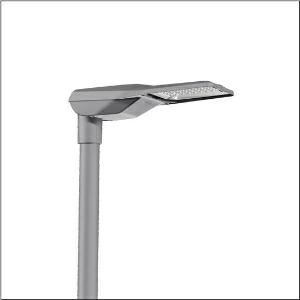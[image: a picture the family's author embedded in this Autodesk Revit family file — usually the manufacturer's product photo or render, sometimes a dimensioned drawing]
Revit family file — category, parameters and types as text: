
# Revit family: streetlight_sl_21_iq_mini___st1_0a_5xe2d21g08hb_8dd2
name_source: partatom
category: Lighting Fixtures
units: mm (PartAtom-declared; Revit-internal decimal feet)

## family parameters
Cut with Voids When Loaded = No
Host = Face
Light Source = No
Part Type = Normal
Room Calculation Point = No
Round Connector Dimension = Use Diameter
Shared = No

## types (1)
- --- (1 x LED, 7830 lm, 70.9 W, 2200K)
    Apparent Load = 71 VA
    CIE Flux Codes = 37 72 97 100 100
    Color Rendering = 70
    Color Temperature = 2200K
    Default Elevation = 1800 mm
    Description = Streetlight SL 21 iQ mini, mast luminaire, primary light control with lens, of PMMA, primary optical cover: cover, of toughened safety glass, transparent, light distribution: ST1.0a, light emission: direct distribution, primary light characteristic: asymmetric, installation type: post-top, side-entry, LED, High Power LED, rated luminous flux: 7.830lm, luminous efficacy: 110lm/W, light colour: 722, colour temperature: 2200K, control: Street-Remote, Auto-Match, Temp-Guard, Lumen-Switch, Night-Set, Smart-Wire, Light-Fading, Desk-Remote (wireless, voltage-free reading and setting of iQ features in the workshop via application-optimized NFC function/RFID function), optimised constant luminous flux control (CLO 2.0), pre-setting: linear dimming characteristic, mains connection: 220..240V, AC, 50/60Hz, start of lifetime: 71W, end of service life: 75W, reduction: 31W, luminaire housing, of diecast aluminium, powder-coated, Siteco® metallic grey (DB 702S), corrosivity category C5 mid according to DIN EN ISO 12944, please order mast flange separately, inclination adjustable: 0°, 5°, 10°, 15°, sealing non-destructively replaceable, multi-level sealing system, length: 628mm, width: 235mm, height: 110mm, mast flange for spigot size: 42mm (side-entry): 5XC10008XM4, 60/48mm (side-entry/post-top): 5XC10108XM2, 76/60mm (side-entry/post-top): 5XC10108XM1, protection rating (complete): IP66, insulation class (complete): insulation class II (safety insulation), certification: CE, ENEC, ENEC+, VDE, impact resistance: IK09, permissible operating ambient temperature for outdoor applications: -40..+50°C, standard-compliant lighting for roads and squares, packaging unit: 1 piece

Light Distribution: ST1.0a
    Height = 110 mm
    Lamp = 1 x LED
    Lamp Light Flux = 7830 lm
    Lamp Power = 70.9 W
    Lamp count = 1
    Length = 625 mm
    Luminous efficacy = 110 lm/W
    Manufacturer = Siteco
    ModVariant = No
    Model = 5XE2D21G08HB
    Number of Poles = 1
    OnlyDefault = Yes
    Power Factor = 1
    Product Name = Streetlight SL 21 iQ mini | ST1.0a
    Product group = mast luminaire | pylon top
    ProductGroupID = 6100
    Protection Class = Protection class II
    Protection Degree = IP 66
    RLX_Detail_Level = 1
    RLX_Emergency_Light_Flux = 0 lm
    RLX_Emergency_Type = 0
    RLX_Emergency_Type_DB = No
    RlxData = <blob elided: 92389 chars, md5=9c6acbc7>
    Socket = socket
    Standby Power = 0 W
    System Light Flux = 7830 lm
    System Power = 71 W
    Type Comments = factory setting: luminous flux: 100 % | dim-lin: 254 | 711 mA
    Type Image = l_1003519.jpg
    URL = http://relux.com
    VarID = @adj_128635
    Voltage = 0 V
    Weight = 0.00 kg
    Width = 234 mm

## geometry (parser evidence)
native form markers: Blend x4, Sweep x12
no freeform markers — native parametric forms only
